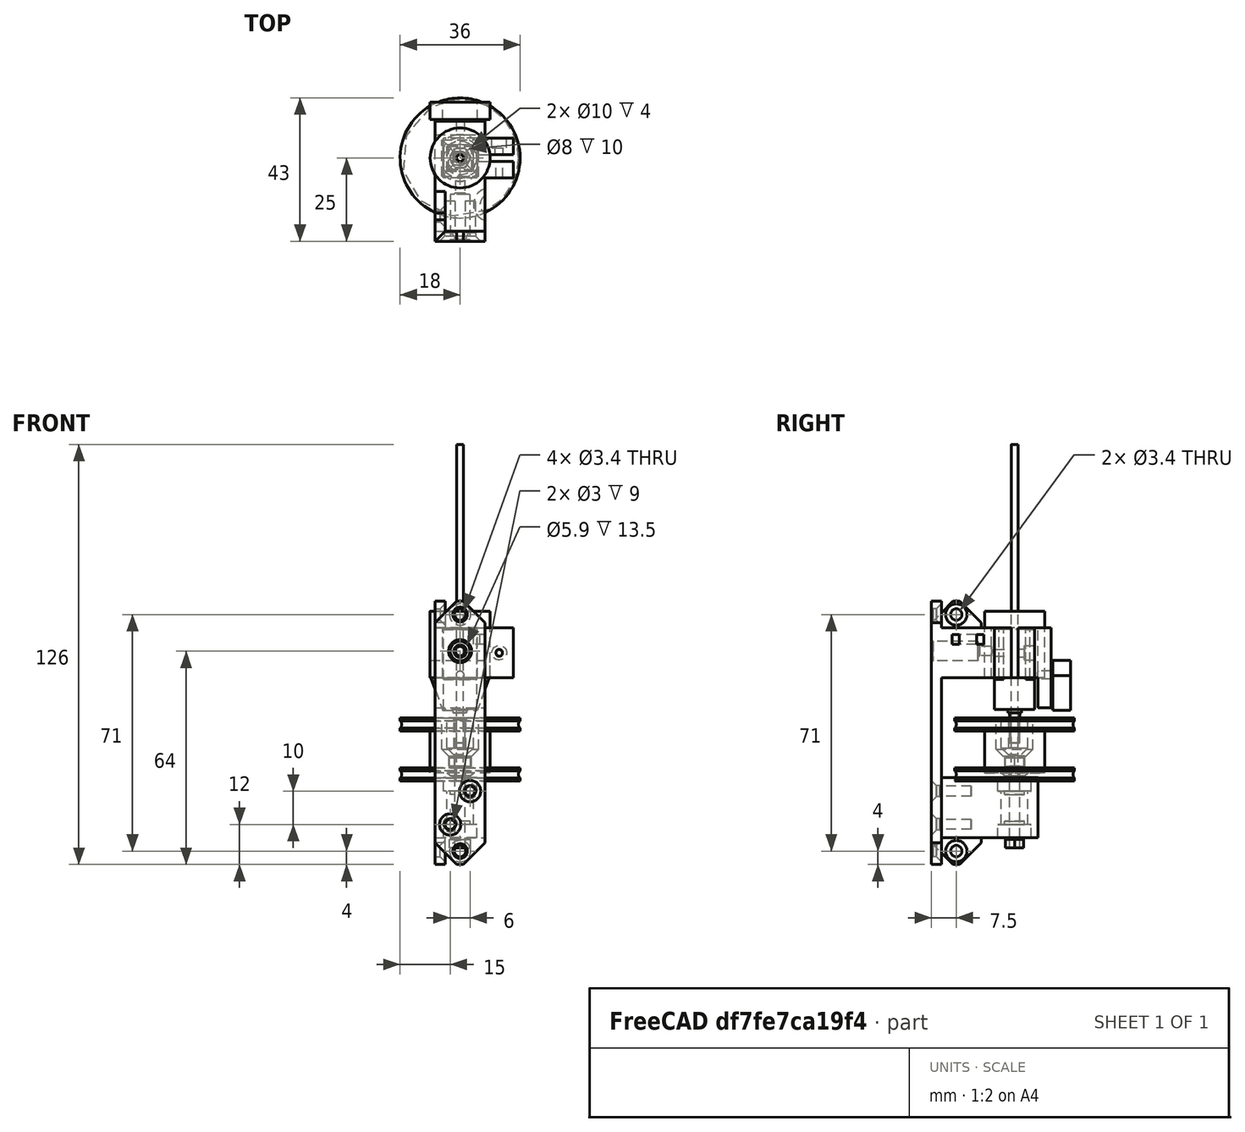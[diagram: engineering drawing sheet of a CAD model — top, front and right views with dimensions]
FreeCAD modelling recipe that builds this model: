
FCSTD DOCUMENT  (FreeCAD 0.18R16146 (Git))
Label: Motor and Opto Sensor Mount0.5
License: All rights reserved
LicenseURL: http://en.wikipedia.org/wiki/All_rights_reserved
objects: Part::Cylinder×36, Part::Cut×26, Part::Box×21, Part::MultiFuse×15, Drawing::FeatureViewAnnotation×15, Part::Chamfer×14, Part::Fuse×4, Part::Feature×3, Part::MultiCommon×2, Part::Torus×2, Part::Mirroring×2, Part::Cone×1, App::DocumentObjectGroup×1, Drawing::FeaturePage×1
note: 126 computed .brp shape members not serialized (recipe doc carries the construction recipe); baked Part::Feature solids carry a one-line shape summary decoded from their .brp

FEATURE [Part::Box] Box406008004  label="gearbox004"
  AttacherType = Attacher::AttachEngine3D
  Height = 9
  Length = 12
  Placement = pos=(-6,-5,0) rot=(0,0,1;0rad)
  Width = 10
FEATURE [Part::Cylinder] Cylinder076  label="boss002"
  Angle = 360
  AttacherType = Attacher::AttachEngine3D
  Height = 1
  Placement = pos=(0,0,-1) rot=(0,0,1;0rad)
  Radius = 2
FEATURE [Part::Cylinder] Cylinder077
  Angle = 360
  AttacherType = Attacher::AttachEngine3D
  Height = 15
  Placement = pos=(0,0,9) rot=(0,0,1;0rad)
  Radius = 6
FEATURE [Part::Box] Box406008005  label="gearbox005"
  AttacherType = Attacher::AttachEngine3D
  Height = 27
  Length = 16
  Placement = pos=(-8,-5,0) rot=(0,0,1;0rad)
  Width = 10
FEATURE [Part::MultiCommon] Common001  label="motor002"
  Shapes = -> [Cylinder077,Box406008005]
FEATURE [Part::Cylinder] Cylinder078  label="shaft-002"
  Angle = 360
  AttacherType = Attacher::AttachEngine3D
  Height = 10
  Placement = pos=(0,0,-10) rot=(0,0,1;0rad)
  Radius = 1.5
FEATURE [Part::Box] Box406008006  label="Cube341"
  AttacherType = Attacher::AttachEngine3D
  Height = 12
  Length = 10
  Placement = pos=(-5,1,-11) rot=(0,0,1;0rad)
  Width = 10
FEATURE [Part::Cut] Cut001  label="shaft002"
  Base = -> Cylinder078
  Tool = -> Box406008006
FEATURE [Part::MultiFuse] Fusion103077013004017004  label="motor-assembled"
  Placement = pos=(0,0,20.5) rot=(0,0,1;1.5708rad)
  Shapes = -> [Box406008004,Cylinder076,Common001,Cut001]
FEATURE [Part::Cylinder] Cylinder028  label="Cylinder024"
  Angle = 360
  AttacherType = Attacher::AttachEngine3D
  Height = 10
  Placement = pos=(0,0,-1) rot=(0,0,1;0rad)
  Radius = 1.57
FEATURE [Part::Cylinder] Cylinder012  label="wheel1a"
  Angle = 360
  AttacherType = Attacher::AttachEngine3D
  Height = 4
  Radius = 18
FEATURE [Part::Box] Box084016  label="Cube067"
  AttacherType = Attacher::AttachEngine3D
  Height = 12
  Length = 10
  Placement = pos=(-5,1.1,-1.5) rot=(0,0,1;0rad)
  Width = 10
FEATURE [Part::Torus] Torus002
  Angle1 = -180
  Angle2 = 180
  Angle3 = 360
  AttacherType = Attacher::AttachEngine3D
  Placement = pos=(0,0,2) rot=(0,0,1;0rad)
  Radius1 = 19
  Radius2 = 1.5
FEATURE [Part::Cut] Cut057
  Base = -> Cylinder028
  Tool = -> Box084016
FEATURE [Part::Cut] Cut062
  Base = -> Cylinder012
  Tool = -> Cut057
FEATURE [Part::Cut] Cut063  label="wheel 0.1"
  Base = -> Cut062
  Placement = pos=(0,0,-1) rot=(0,0,1;0rad)
  Tool = -> Torus002
FEATURE [Part::Cylinder] Cylinder073  label="motor-bulge"
  Angle = 360
  AttacherType = Attacher::AttachEngine3D
  Height = 20
  Placement = pos=(0,0,30) rot=(0,0,1;0rad)
  Radius = 9
FEATURE [Part::Cylinder] Cylinder067
  Angle = 360
  AttacherType = Attacher::AttachEngine3D
  Height = 26
  Placement = pos=(0,0,20) rot=(0,0,1;0rad)
  Radius = 7
FEATURE [Part::Box] Box406017  label="gearbox001"
  AttacherType = Attacher::AttachEngine3D
  Height = 28
  Length = 16
  Placement = pos=(-8,-5.25,18) rot=(0,0,1;0rad)
  Width = 10.5
FEATURE [Part::MultiCommon] Common004  label="motor-hole"
  Placement = pos=(0,0,5) rot=(0,0,1;1.5708rad)
  Shapes = -> [Cylinder067,Box406017]
FEATURE [Part::Box] Box406016  label="clamp-slot"
  AttacherType = Attacher::AttachEngine3D
  Height = 32
  Length = 49
  Placement = pos=(48.48,1,22) rot=(0,0,1;3.14159rad)
  Width = 2
FEATURE [Part::Box] Box  label="Cube"
  AttacherType = Attacher::AttachEngine3D
  Height = 8
  Length = 15
  Placement = pos=(-7.5,-25,45) rot=(0,0,1;0rad)
  Width = 3
FEATURE [Part::Box] Box406008007  label="Cube342"
  AttacherType = Attacher::AttachEngine3D
  Height = 14.9
  Length = 18
  Placement = pos=(-9,13,34.3) rot=(0,0,1;0rad)
  Width = 5.3
FEATURE [Part::Cylinder] Cylinder079  label="Cylinder078"
  Angle = 360
  AttacherType = Attacher::AttachEngine3D
  Height = 17
  Placement = pos=(0,0,9) rot=(0,0,1;0rad)
  Radius = 1.75
FEATURE [Part::Box] Box406008008  label="Cube343"
  AttacherType = Attacher::AttachEngine3D
  Height = 19
  Length = 10
  Placement = pos=(-5,1.1,1.5) rot=(0,0,1;0rad)
  Width = 10
FEATURE [Part::Cut] Cut064  label="Motor Shaft Hole"
  Base = -> Cylinder079
  Tool = -> Box406008008
FEATURE [Part::Box] Box406008009  label="Cube344"
  AttacherType = Attacher::AttachEngine3D
  Height = 11
  Length = 8
  Placement = pos=(-4,-4,7) rot=(0,0,1;0rad)
  Width = 8
FEATURE [Part::Box] Box406008010  label="Cube345"
  AttacherType = Attacher::AttachEngine3D
  Height = 19.7
  Length = 17.5
  Placement = pos=(3.75,6,30.3) rot=(0,1,0;0.349066rad)
  Width = 13.3
FEATURE [Part::Box] Box406008011  label="Cube346"
  AttacherType = Attacher::AttachEngine3D
  Height = 19.7
  Length = 17.5
  Placement = pos=(3.75,6,30.3) rot=(0,1,0;0.349066rad)
  Width = 13.3
FEATURE [Part::Mirroring] Part__Mirroring  label="Cube346 (Mirror #1)"
  Base = (0,0,0)
  Normal = (1,0,0)
  Source = -> Box406008011
FEATURE [Part::MultiFuse] Fusion
  Shapes = -> [Box406008010,Part__Mirroring]
FEATURE [Part::Cut] Cut  label="Opto Sensor"
  Base = -> Box406008007
  Placement = pos=(0,-1.5,-14) rot=(0,0,1;0rad)
  Tool = -> Fusion
FEATURE [Part::Cut] Cut065  label="Square Peg"
  Base = -> Box406008009
  Tool = -> Cut064
FEATURE [Part::Box] Box406008012  label="Cube347"
  AttacherType = Attacher::AttachEngine3D
  Height = 11.5
  Length = 11
  Placement = pos=(-5.5,-5.5,6.5) rot=(0,0,1;0rad)
  Width = 11
FEATURE [Part::Cylinder] Cylinder
  Angle = 360
  AttacherType = Attacher::AttachEngine3D
  Height = 12.5
  Placement = pos=(0,0,1.5) rot=(0,0,1;0rad)
  Radius = 9
FEATURE [Part::Cylinder] Cylinder080  label="wheel1a001"
  Angle = 360
  AttacherType = Attacher::AttachEngine3D
  Height = 4
  Placement = pos=(0,0,14) rot=(0,0,1;0rad)
  Radius = 18
FEATURE [Part::Feature] Shape
  Placement = pos=(0,0,3.5) rot=(0,0,1;0rad)
  shape: bbox 6.697 x 5.8 x 15 mm, 8 faces (baked)
FEATURE [Part::MultiFuse] Fusion103077013004017005
  Shapes = -> [Cylinder080,Cylinder]
FEATURE [Part::Feature] Shape001
  Placement = pos=(0,0,3.5) rot=(0,0,1;0rad)
  shape: bbox 6.351 x 5.5 x 2.5 mm, 8 faces (baked)
FEATURE [Part::Cylinder] Cylinder081  label="Cylinder079"
  Angle = 360
  AttacherType = Attacher::AttachEngine3D
  Height = 25
  Placement = pos=(0,0,-21) rot=(0,0,1;0rad)
  Radius = 1.5
FEATURE [Part::MultiFuse] Fusion103077013004017006  label="M3 x 25 Hex Head"
  Shapes = -> [Shape001,Cylinder081]
FEATURE [Part::Cut] Cut066
  Base = -> Fusion103077013004017005
  Tool = -> Box406008012
FEATURE [Part::Cone] Cone
  Angle = 360
  AttacherType = Attacher::AttachEngine3D
  Height = 1
  Placement = pos=(0,0,0.5) rot=(0,0,1;0rad)
  Radius1 = 3
  Radius2 = 4
FEATURE [Part::MultiFuse] Fusion103077013004017007
  Shapes = -> [Cut066,Cone]
FEATURE [Part::Cut] Cut067
  Base = -> Fusion103077013004017007
  Tool = -> Shape
FEATURE [Part::Cylinder] Cylinder082  label="623 Bearing"
  Angle = 360
  AttacherType = Attacher::AttachEngine3D
  Height = 4
  Placement = pos=(0,0,-4) rot=(0,0,1;0rad)
  Radius = 5
FEATURE [Part::Cylinder] Cylinder083  label="623 Bearing001"
  Angle = 360
  AttacherType = Attacher::AttachEngine3D
  Height = 4
  Placement = pos=(0,0,-18) rot=(0,0,1;0rad)
  Radius = 5
FEATURE [Part::Feature] Shape002  label="Nylock"
  Placement = pos=(0,0,-21) rot=(0,0,1;0rad)
  shape: bbox 6.351 x 5.5 x 2.5 mm, 8 faces (baked)
FEATURE [Part::Cylinder] Cylinder084  label="Cylinder080"
  Angle = 360
  AttacherType = Attacher::AttachEngine3D
  Height = 6
  Placement = pos=(0,0,-2) rot=(0,0,1;0rad)
  Radius = 1.5
FEATURE [Part::Cut] Cut069
  Base = -> Cut067
  Tool = -> Cylinder084
FEATURE [Part::Cylinder] Cylinder085  label="Cylinder081"
  Angle = 360
  AttacherType = Attacher::AttachEngine3D
  Height = 19
  Placement = pos=(0,0,-17) rot=(0,0,1;0rad)
  Radius = 4
FEATURE [Part::Box] Box406008013  label="Cube348"
  AttacherType = Attacher::AttachEngine3D
  Height = 18
  Length = 15
  Placement = pos=(-7.5,-22,-18) rot=(0,0,1;0rad)
  Width = 29
FEATURE [Part::Cylinder] Cylinder086  label="623 Bearing002"
  Angle = 360
  AttacherType = Attacher::AttachEngine3D
  Height = 4
  Placement = pos=(0,0,-4) rot=(0,0,1;0rad)
  Radius = 5
FEATURE [Part::Cylinder] Cylinder087  label="623 Bearing003"
  Angle = 360
  AttacherType = Attacher::AttachEngine3D
  Height = 4
  Placement = pos=(0,0,-18) rot=(0,0,1;0rad)
  Radius = 5
FEATURE [Part::MultiFuse] Fusion103077013004017008  label="623 Bearing Holes"
  Shapes = -> [Cylinder086,Cylinder087]
FEATURE [Part::Cut] Cut070
  Base = -> Box406008013
  Tool = -> Fusion103077013004017008
FEATURE [Part::Cylinder] Cylinder088  label="Cylinder082"
  Angle = 360
  AttacherType = Attacher::AttachEngine3D
  Height = 1
  Placement = pos=(0,0,-5) rot=(0,0,1;0rad)
  Radius = 3
FEATURE [Part::Cylinder] Cylinder089  label="Cylinder083"
  Angle = 360
  AttacherType = Attacher::AttachEngine3D
  Height = 1
  Placement = pos=(0,0,-14) rot=(0,0,1;0rad)
  Radius = 3
FEATURE [Part::MultiFuse] Fusion103077013004017009
  Shapes = -> [Cylinder089,Cylinder088]
FEATURE [Part::Box] Box406008014  label="Cube349"
  AttacherType = Attacher::AttachEngine3D
  Height = 63
  Length = 15
  Placement = pos=(-7.5,-25,-18) rot=(0,0,1;0rad)
  Width = 3
FEATURE [Part::Box] Box406008015  label="Cube350"
  AttacherType = Attacher::AttachEngine3D
  Height = 15
  Length = 15
  Placement = pos=(-7.5,-22,35) rot=(0,0,1;0rad)
  Width = 31
FEATURE [Part::Cut] Cut073
  Base = -> Box406008015
  Tool = -> Common004
FEATURE [Part::Cylinder] Cylinder068
  Angle = 360
  AttacherType = Attacher::AttachEngine3D
  Height = 12
  Placement = pos=(11.75,0,42.5) rot=(0,0.707106,0.707107;3.14159rad)
  Radius = 1.2
FEATURE [Part::Cylinder] Cylinder069
  Angle = 360
  AttacherType = Attacher::AttachEngine3D
  Height = 12
  Placement = pos=(11.75,3,42.5) rot=(0,0.707106,0.707107;3.14159rad)
  Radius = 2.2
FEATURE [Part::MultiFuse] Fusion103077013  label="M2-screw001"
  Shapes = -> [Cylinder068,Cylinder069]
FEATURE [Part::Box] Box406008016  label="Cube351"
  AttacherType = Attacher::AttachEngine3D
  Height = 15
  Length = 9
  Placement = pos=(7,-6,35) rot=(0,0,1;0rad)
  Width = 12
FEATURE [Part::Fuse] Fusion103077013004017010
  Base = -> Cut073
  Tool = -> Box406008016
FEATURE [Part::Cut] Cut074
  Base = -> Fusion103077013004017010
  Tool = -> Box406016
FEATURE [Part::Box] Box406008017  label="Cube352"
  AttacherType = Attacher::AttachEngine3D
  Height = 24
  Length = 15
  Placement = pos=(-7.5,7,26) rot=(0,0,1;0rad)
  Width = 4
FEATURE [Part::Cylinder] Cylinder090  label="Cylinder084"
  Angle = 360
  AttacherType = Attacher::AttachEngine3D
  Height = 13
  Placement = pos=(0,16,35.8) rot=(1,0,0;1.5708rad)
  Radius = 1.2
FEATURE [Part::Cylinder] Cylinder091
  Angle = 360
  AttacherType = Attacher::AttachEngine3D
  Height = 12
  Placement = pos=(11.75,-12,42.5) rot=(0,0.707106,0.707107;3.14159rad)
  Radius = 1
FEATURE [Part::Fuse] Fusion103077013004017011
  Base = -> Fusion103077013
  Tool = -> Cylinder091
FEATURE [Part::Cut] Cut075
  Base = -> Cut074
  Tool = -> Fusion103077013004017011
FEATURE [Part::Fuse] Fusion103077013004017012
  Base = -> Box406008017
  Tool = -> Cut075
FEATURE [Part::Cut] Cut076  label="Motor Mount 0.2"
  Base = -> Fusion103077013004017012
  Placement = pos=(0,0,-5) rot=(0,0,1;0rad)
  Tool = -> Cylinder090
FEATURE [Part::Cylinder] Cylinder092
  Angle = 360
  AttacherType = Attacher::AttachEngine3D
  Height = 21
  Placement = pos=(-3,-13,-14) rot=(1,0,0;1.5708rad)
  Radius = 1.7
FEATURE [Part::Cylinder] Cylinder093
  Angle = 360
  AttacherType = Attacher::AttachEngine3D
  Height = 21
  Placement = pos=(3,-13,-4) rot=(1,0,0;1.5708rad)
  Radius = 1.7
FEATURE [Part::Cylinder] Cylinder094
  Angle = 360
  AttacherType = Attacher::AttachEngine3D
  Height = 21
  Placement = pos=(-3,-13,-14) rot=(1,0,0;1.5708rad)
  Radius = 1.5
FEATURE [Part::Cylinder] Cylinder095
  Angle = 360
  AttacherType = Attacher::AttachEngine3D
  Height = 21
  Placement = pos=(3,-13,-4) rot=(1,0,0;1.5708rad)
  Radius = 1.5
FEATURE [Part::MultiFuse] Fusion103077013004017013
  Shapes = -> [Cylinder092,Cylinder093]
FEATURE [Part::Cut] Cut077
  Base = -> Box406008014
  Tool = -> Fusion103077013004017013
FEATURE [Part::MultiFuse] Fusion103077013004017014
  Shapes = -> [Cylinder094,Cylinder095]
FEATURE [Part::Cylinder] Cylinder096
  Angle = 360
  AttacherType = Attacher::AttachEngine3D
  Height = 21
  Placement = pos=(0,-13,49) rot=(1,0,0;1.5708rad)
  Radius = 1.7
FEATURE [Part::Cylinder] Cylinder097
  Angle = 360
  AttacherType = Attacher::AttachEngine3D
  Height = 21
  Placement = pos=(0,-13,-22) rot=(1,0,0;1.5708rad)
  Radius = 1.7
FEATURE [Part::Chamfer] Chamfer003  label="Wheel"
  Base = -> Cut069
  Edges = 4 edges r=2: [Edge11,Edge12,Edge15,Edge16]
FEATURE [Part::Chamfer] Chamfer004  label="Square Peg001"
  Base = -> Cut065
  Edges = 4 edges r=2: [Edge4,Edge5,Edge13,Edge15]
FEATURE [Part::Box] Box406008018  label="Cube353"
  AttacherType = Attacher::AttachEngine3D
  Height = 8
  Length = 15
  Placement = pos=(-7.5,-25,-26) rot=(0,0,1;0rad)
  Width = 3
FEATURE [Part::Cut] Cut079
  Base = -> Box406008018
  Tool = -> Cylinder097
FEATURE [Part::Cut] Cut080
  Base = -> Box
  Tool = -> Cylinder096
FEATURE [Part::MultiFuse] Fusion103077013004017015
  Shapes = -> [Cut079,Cut080]
FEATURE [Part::Chamfer] Chamfer005  label="Chamfer005 mount holes"
  Base = -> Fusion103077013004017015
  Edges = 2 edges r=1.5: [Edge13,Edge28]
FEATURE [Part::Chamfer] Chamfer006  label="Chamfer under side CS screw holes"
  Base = -> Cut077
  Edges = 2 edges r=1.5: [Edge8,Edge9]
FEATURE [Part::MultiFuse] Fusion103077013004017016
  Shapes = -> [Chamfer006,Chamfer005]
FEATURE [Part::Chamfer] Chamfer007  label="Chamfer Corner edges of mount"
  Base = -> Fusion103077013004017016
  Edges = 4 edges r=6.5: [Edge27,Edge29,Edge34,Edge39]
FEATURE [Part::Cylinder] Cylinder098
  Angle = 360
  AttacherType = Attacher::AttachEngine3D
  Height = 3
  Placement = pos=(-9,-9,36) rot=(1,0,0;0rad)
  Radius = 5
FEATURE [Part::Cylinder] Cylinder099
  Angle = 360
  AttacherType = Attacher::AttachEngine3D
  Height = 3
  Placement = pos=(-9,-9,36) rot=(1,0,0;0rad)
  Radius = 3
FEATURE [Part::Cut] Cut081  label="Cable tie Hole"
  Base = -> Cylinder098
  Placement = pos=(18,-5,4) rot=(0,0,1;0rad)
  Tool = -> Cylinder099
FEATURE [Part::Cut] Cut082
  Base = -> Cut076
  Tool = -> Cut081
FEATURE [Part::MultiFuse] Fusion103077013004017017
  Shapes = -> [Chamfer007,Cut082]
FEATURE [Drawing::FeatureViewAnnotation] Annotation
  Font = Sans
  Rotation = 0
  Scale = 7
  Text = Square Peg 0.1 - 0.2 Hole R 1.57 -> 1.75 and chamfered
  ViewResult = <g transform="translate(10,20) rotate(0)">\n<text id="Annotation"\n font-family="Sans"\n font-size="7"\n fill="#000000">\n<tspan x="0" dy="1em">Square Peg 0.1 - 0.2 Hole R 1.57 -> 1.75 and chamfered</tspan>\n</text>\n</g>
  Visible = true
  X = 10
  Y = 20
FEATURE [Part::Chamfer] Chamfer008  label="Square Peg 0.3"
  Base = -> Chamfer004
  Edges = 3 edges r=0.5: [Edge13,Edge14,Edge15]
FEATURE [Drawing::FeatureViewAnnotation] Annotation001
  Font = Sans
  Rotation = 0
  Scale = 7
  Text = Bearing Mount End 0.2 0 Hole R 1.5 -> 1.8
  ViewResult = <g transform="translate(20,40) rotate(0)">\n<text id="Annotation001"\n font-family="Sans"\n font-size="7"\n fill="#000000">\n<tspan x="0" dy="1em">Bearing Mount End 0.2 0 Hole R 1.5 -> 1.8</tspan>\n</text>\n</g>
  Visible = true
  X = 20
  Y = 40
FEATURE [Drawing::FeatureViewAnnotation] Annotation002
  Font = Sans
  Rotation = 0
  Scale = 7
  Text = Motor Mount Hole 6.25 -> 7mm
  ViewResult = <g transform="translate(20,30) rotate(0)">\n<text id="Annotation002"\n font-family="Sans"\n font-size="7"\n fill="#000000">\n<tspan x="0" dy="1em">Motor Mount Hole 6.25 -> 7mm</tspan>\n</text>\n</g>
  Visible = true
  X = 20
  Y = 30
FEATURE [Part::Chamfer] Chamfer009  label="Chamfer on bottom of mount holes (so they print better)"
  Base = -> Fusion103077013004017017
  Edges = 2 edges r=0.5: [Edge46,Edge47]
FEATURE [Part::Chamfer] Chamfer010  label="Motor and Opto Sensor Mount 0.2"
  Base = -> Chamfer009
  Edges = 2 edges r=0.5: [Edge102,Edge107]
FEATURE [Drawing::FeatureViewAnnotation] Annotation003
  Font = Sans
  Rotation = 0
  Scale = 7
  Text = Chamfered holes that are printed sideways
  ViewResult = <g transform="translate(20,50) rotate(0)">\n<text id="Annotation003"\n font-family="Sans"\n font-size="7"\n fill="#000000">\n<tspan x="0" dy="1em">Chamfered holes that are printed sideways</tspan>\n</text>\n</g>
  Visible = true
  X = 20
  Y = 50
FEATURE [Part::Cylinder] Cylinder100
  Angle = 360
  AttacherType = Attacher::AttachEngine3D
  Height = 28
  Placement = pos=(0,0,38) rot=(1,0,0;1.5708rad)
  Radius = 1.4
FEATURE [Drawing::FeatureViewAnnotation] Annotation004
  Font = Sans
  Rotation = 0
  Scale = 7
  Text = 0.2 -> 0.3 Changes
  ViewResult = <g transform="translate(10,70) rotate(0)">\n<text id="Annotation004"\n font-family="Sans"\n font-size="7"\n fill="#000000">\n<tspan x="0" dy="1em">0.2 -> 0.3 Changes</tspan>\n</text>\n</g>
  Visible = true
  X = 10
  Y = 70
FEATURE [Drawing::FeatureViewAnnotation] Annotation005
  Font = Sans
  Rotation = 0
  Scale = 7
  Text = Hole to hold motor
  ViewResult = <g transform="translate(20,80) rotate(0)">\n<text id="Annotation005"\n font-family="Sans"\n font-size="7"\n fill="#000000">\n<tspan x="0" dy="1em">Hole to hold motor</tspan>\n</text>\n</g>
  Visible = true
  X = 20
  Y = 80
FEATURE [Part::Cylinder] Cylinder101
  Angle = 360
  AttacherType = Attacher::AttachEngine3D
  Height = 20
  Placement = pos=(0,-11,38) rot=(1,0,0;1.5708rad)
  Radius = 2.95
FEATURE [Part::MultiFuse] Fusion103077013004017018
  Shapes = -> [Cylinder100,Cylinder101]
FEATURE [Part::Cylinder] Cylinder102
  Angle = 360
  AttacherType = Attacher::AttachEngine3D
  Height = 21
  Placement = pos=(-15,-17.5,-22) rot=(0,1,0;1.5708rad)
  Radius = 1.7
FEATURE [Part::Box] Box406008019  label="Cube354"
  AttacherType = Attacher::AttachEngine3D
  Height = 8
  Length = 15
  Placement = pos=(-4.5,-25,-26) rot=(0,0,1;1.5708rad)
  Width = 3
FEATURE [Part::Cut] Cut083
  Base = -> Box406008019
  Tool = -> Cylinder102
FEATURE [Part::Chamfer] Chamfer011  label="Chamfer Mount corner edges"
  Base = -> Cut083
  Edges = 2 edges r=6.5: [Edge4,Edge14]
FEATURE [Part::Chamfer] Chamfer012  label="Chamfer012 Mount Hole"
  Base = -> Chamfer011
  Edges = 1 edges r=1.5: [Edge10]
FEATURE [Part::Cylinder] Cylinder103
  Angle = 360
  AttacherType = Attacher::AttachEngine3D
  Height = 21
  Placement = pos=(-15,-17.5,-22) rot=(0,1,0;1.5708rad)
  Radius = 1.7
FEATURE [Part::Box] Box406008020  label="Cube355"
  AttacherType = Attacher::AttachEngine3D
  Height = 8
  Length = 15
  Placement = pos=(-4.5,-25,-26) rot=(0,0,1;1.5708rad)
  Width = 3
FEATURE [Part::Cut] Cut084
  Base = -> Box406008020
  Tool = -> Cylinder103
FEATURE [Part::Chamfer] Chamfer013  label="Chamfer Mount corner edges001"
  Base = -> Cut084
  Edges = 2 edges r=6.5: [Edge4,Edge14]
FEATURE [Part::Chamfer] Chamfer014  label="Chamfer012 Mount Hole001"
  Base = -> Chamfer013
  Edges = 1 edges r=1.5: [Edge10]
FEATURE [Part::Mirroring] Part__Mirroring001  label="Chamfer012 Mount Hole001 (Mirror #2)"
  Base = (0,0,0)
  Normal = (0,0,1)
  Placement = pos=(0,0,27) rot=(0,0,1;0rad)
  Source = -> Chamfer014
FEATURE [Drawing::FeatureViewAnnotation] Annotation006
  Font = Sans
  Rotation = 0
  Scale = 7
  Text = Additional mounts at 90 degrees
  ViewResult = <g transform="translate(20,90) rotate(0)">\n<text id="Annotation006"\n font-family="Sans"\n font-size="7"\n fill="#000000">\n<tspan x="0" dy="1em">Additional mounts at 90 degrees</tspan>\n</text>\n</g>
  Visible = true
  X = 20
  Y = 90
FEATURE [Drawing::FeatureViewAnnotation] Annotation007
  Font = Sans
  Rotation = 0
  Scale = 7
  Text = Switched Cable tie hole and offset
  ViewResult = <g transform="translate(20,100) rotate(0)">\n<text id="Annotation007"\n font-family="Sans"\n font-size="7"\n fill="#000000">\n<tspan x="0" dy="1em">Switched Cable tie hole and offset</tspan>\n</text>\n</g>
  Visible = true
  X = 20
  Y = 100
FEATURE [Part::Cut] Cut085
  Base = -> Chamfer010
  Tool = -> Fusion103077013004017018
FEATURE [Part::MultiFuse] Fusion103077013004017019
  Shapes = -> [Part__Mirroring001,Chamfer012]
FEATURE [Part::Fuse] Fusion103077013004017020
  Base = -> Cut085
  Tool = -> Fusion103077013004017019
FEATURE [Part::Chamfer] Chamfer015
  Base = -> Fusion103077013004017020
  Edges = 1 edges r=0.5: [Edge97]
FEATURE [Part::Chamfer] Chamfer016  label="Motor and Opto Sensor Mount 0.4"
  Base = -> Chamfer015
  Edges = 1 edges r=0.5: [Edge5]
FEATURE [Part::Torus] Torus003
  Angle1 = -180
  Angle2 = 180
  Angle3 = 360
  AttacherType = Attacher::AttachEngine3D
  Placement = pos=(0,0,16) rot=(0,0,1;0rad)
  Radius1 = 19
  Radius2 = 1.5
FEATURE [Part::Cut] Cut086  label="Wheel 0.4"
  Base = -> Chamfer003
  Tool = -> Torus003
FEATURE [Drawing::FeatureViewAnnotation] Annotation008
  Font = Sans
  Rotation = 0
  Scale = 7
  Text = 0.3->0.4
  ViewResult = <g transform="translate(10,120) rotate(0)">\n<text id="Annotation008"\n font-family="Sans"\n font-size="7"\n fill="#000000">\n<tspan x="0" dy="1em">0.3->0.4</tspan>\n</text>\n</g>
  Visible = true
  X = 10
  Y = 120
FEATURE [Drawing::FeatureViewAnnotation] Annotation009
  Font = Sans
  Rotation = 0
  Scale = 7
  Text = Added (subtracted) Torus from the wheel
  ViewResult = <g transform="translate(20,130) rotate(0)">\n<text id="Annotation009"\n font-family="Sans"\n font-size="7"\n fill="#000000">\n<tspan x="0" dy="1em">Added (subtracted) Torus from the wheel</tspan>\n</text>\n</g>
  Visible = true
  X = 20
  Y = 130
FEATURE [Drawing::FeatureViewAnnotation] Annotation010
  Font = Sans
  Rotation = 0
  Scale = 7
  Text = Changed S. Tapping hole on Motor Mount End from 1.7 to 1.4  
  ViewResult = <g transform="translate(20,140) rotate(0)">\n<text id="Annotation010"\n font-family="Sans"\n font-size="7"\n fill="#000000">\n<tspan x="0" dy="1em">Changed S. Tapping hole on Motor Mount End from 1.7 to 1.4  </tspan>\n</text>\n</g>
  Visible = true
  X = 20
  Y = 140
FEATURE [Part::Cut] Cut087
  Base = -> Cut070
  Tool = -> Cylinder085
FEATURE [Part::Cut] Cut088  label="Bearing Mount End 0.5"
  Base = -> Cut087
  Tool = -> Fusion103077013004017014
FEATURE [App::DocumentObjectGroup] Group  label="Old"
  Group = -> [Fusion103077013004017009]
FEATURE [Drawing::FeatureViewAnnotation] Annotation011
  Font = Sans
  Rotation = 0
  Scale = 7
  Text = 0.4>0.5
  ViewResult = <g transform="translate(10,160) rotate(0)">\n<text id="Annotation011"\n font-family="Sans"\n font-size="7"\n fill="#000000">\n<tspan x="0" dy="1em">0.4>0.5</tspan>\n</text>\n</g>
  Visible = true
  X = 10
  Y = 160
FEATURE [Drawing::FeatureViewAnnotation] Annotation012
  Font = Sans
  Rotation = 0
  Scale = 7
  Text = Redesign on bearing mount C81 - R1.8>4 and longer
  ViewResult = <g transform="translate(20,170) rotate(0)">\n<text id="Annotation012"\n font-family="Sans"\n font-size="7"\n fill="#000000">\n<tspan x="0" dy="1em">Redesign on bearing mount C81 - R1.8>4 and longer</tspan>\n</text>\n</g>
  Visible = true
  X = 20
  Y = 170
FEATURE [Drawing::FeatureViewAnnotation] Annotation013
  Font = Sans
  Rotation = 0
  Scale = 7
  Text = 623 bearing R 5.5>5
  ViewResult = <g transform="translate(20,180) rotate(0)">\n<text id="Annotation013"\n font-family="Sans"\n font-size="7"\n fill="#000000">\n<tspan x="0" dy="1em">623 bearing R 5.5>5</tspan>\n</text>\n</g>
  Visible = true
  X = 20
  Y = 180
FEATURE [Part::Cylinder] Cylinder104
  Angle = 360
  AttacherType = Attacher::AttachEngine3D
  Height = 100
  Radius = 1
FEATURE [Drawing::FeatureViewAnnotation] Annotation014
  Font = Sans
  Rotation = 0
  Scale = 7
  Text = Square Peg 10mm square reduced to 8mm
  ViewResult = <g transform="translate(20,200) rotate(0)">\n<text id="Annotation014"\n font-family="Sans"\n font-size="7"\n fill="#000000">\n<tspan x="0" dy="1em">Square Peg 10mm square reduced to 8mm</tspan>\n</text>\n</g>
  Visible = true
  X = 20
  Y = 200
FEATURE [Drawing::FeaturePage] Page
  EditableTexts = AUTHOR NAME | CREATION DATE | SUPERVISOR NAME | CHECK DATE | SCALE | WEIGHT | NUMBER | SHEET | TITLE | SUBTITLE
  Group = -> [Annotation,Annotation001,Annotation002,Annotation003,Annotation004,Annotation005,Annotation006,Annotation007,Annotation008,Annotation009,Annotation010,Annotation011,Annotation012,Annotation013,Annotation014]
  Template = <path>
note: 1 file-system path scrubbed to <path> (originals preserved in the JSON sidecar)
